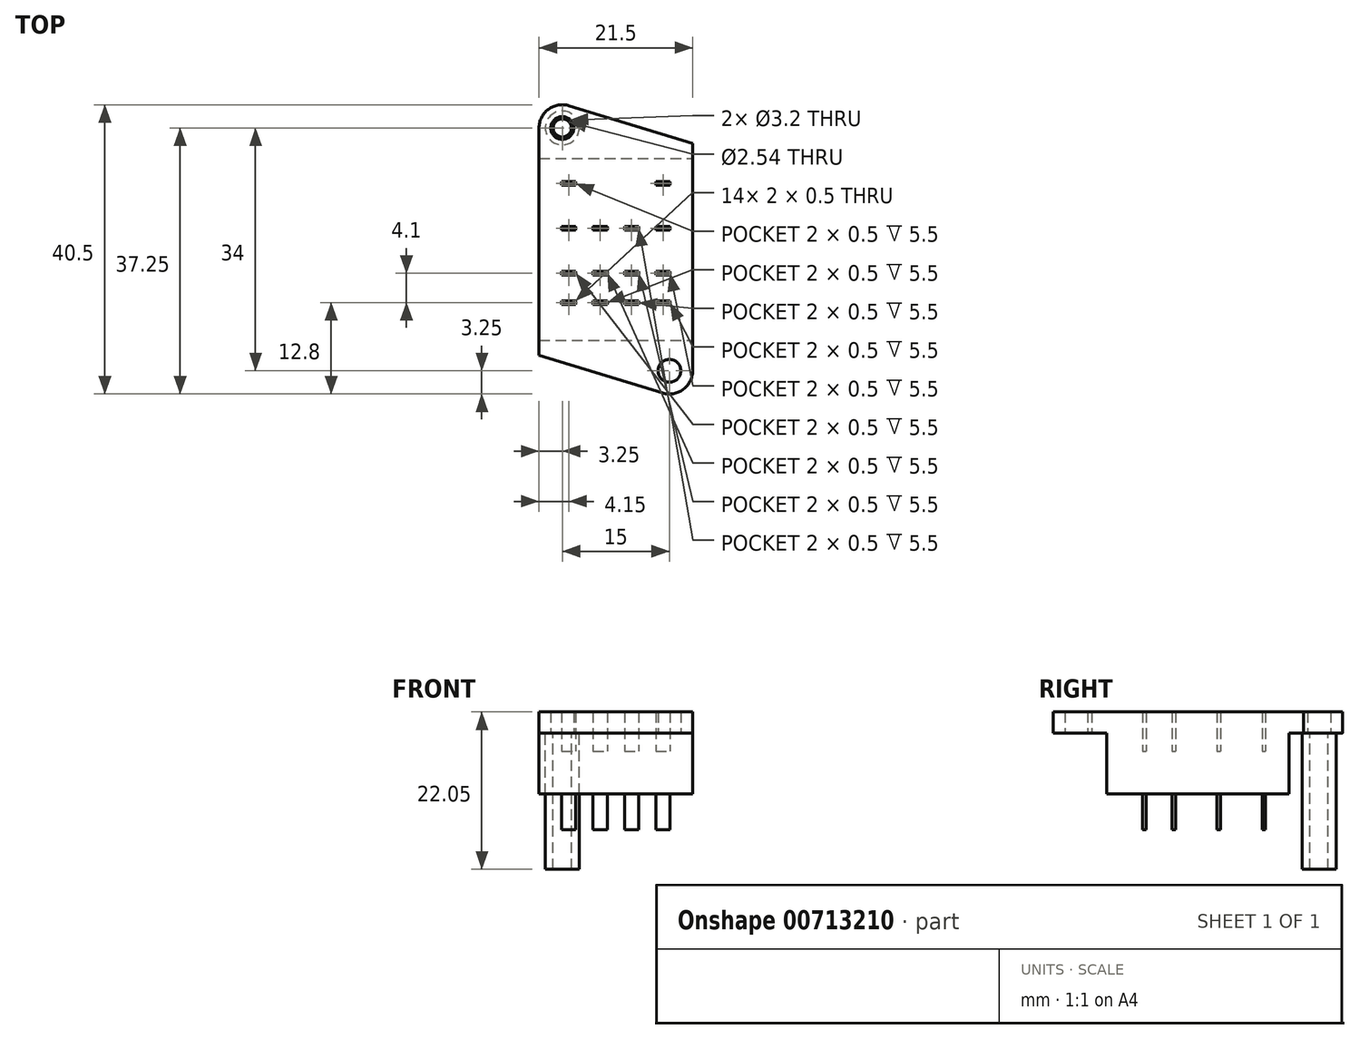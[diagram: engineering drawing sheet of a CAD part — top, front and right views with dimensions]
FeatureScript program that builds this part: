
annotation { "Feature Type Name" : "Feature", "Feature Type Description" : "" }
export const myFeature = defineFeature(function(context is Context, id is Id, definition is map)
    precondition{}
    {
        {
            var Q0;
            Q0=qCreatedBy(makeId("Top.planeOp"),FACE);
            var sketch = newSketch(context, id + "F0", { "sketchPlane" : qUnion([Q0])});
            skLineSegment(sketch, "E0", {"start": v(-10.75, 17) * mm, "end": v(-10.75, -14.82) * mm});
            skLineSegment(sketch, "E1", {"start": v(10.75, 14.82) * mm, "end": v(10.75, -17) * mm});
            skCircle(sketch, "E2", {"center": v(-7.5, 17) * mm, "radius": 1.6 * mm});
            skCircle(sketch, "E3", {"center": v(7.5, -17) * mm, "radius": 1.6 * mm});
            skArc(sketch, "E4", {"start": v(-10.75, 17) * mm, "mid": v(-9.43, 19.61) * mm, "end": v(-6.55, 20.1) * mm});
            skArc(sketch, "E5", {"start": v(10.75, -17) * mm, "mid": v(9.43, -19.61) * mm, "end": v(6.55, -20.1) * mm});
            skLineSegment(sketch, "E6", {"start": v(-10.75, -14.82) * mm, "end": v(6.55, -20.1) * mm});
            skLineSegment(sketch, "E7", {"start": v(-6.55, 20.1) * mm, "end": v(10.75, 14.82) * mm});
            skPoint(sketch, "E8.orphan", {"position": v(-10.75, -22.92) * mm});
            skPoint(sketch, "E9.orphan", {"position": v(15.75, -22.92) * mm});
            skSolve(sketch);
        }
        {
            var Q0;
            Q0 = qSketchRegion(id + "F0", true);
            extrude(context, id + "F1", {"entities" : qUnion([Q0]), "depth" : 3 * mm, "offsetDistance" : 25.4 * mm});
        }
        {
            var Q0;
            Q0=qCreatedBy(makeId("Top.planeOp"),FACE);
            var sketch = newSketch(context, id + "F2", { "sketchPlane" : qUnion([Q0])});
            skLineSegment(sketch, "E10.bottom", {"start": v(-10.75, 12.75) * mm, "end": v(10.75, 12.75) * mm});
            skLineSegment(sketch, "E10.top", {"start": v(-10.75, -12.75) * mm, "end": v(10.75, -12.75) * mm});
            skLineSegment(sketch, "E10.left", {"start": v(-10.75, 12.75) * mm, "end": v(-10.75, -12.75) * mm});
            skLineSegment(sketch, "E10.right", {"start": v(10.75, 12.75) * mm, "end": v(10.75, -12.75) * mm});
            skSolve(sketch);
        }
        {
            var Q0;
            Q0 = qSketchRegion(id + "F2", true);
            extrude(context, id + "F3", {"entities" : qUnion([Q0]), "operationType" : NewBodyOperationType.ADD, "oppositeDirection" : true, "depth" : 8.5 * mm, "offsetDistance" : 25.4 * mm});
        }
        {
            var Q0;
            Q0=makeQuery(id+"F3.opExtrude","CAP_FACE",FACE,{"disambiguationData":[OSD([sQuery(id+"F2.wireOp",EDGE,"E10.bottom"),sQuery(id+"F2.wireOp",EDGE,"E10.top"),sQuery(id+"F2.wireOp",EDGE,"E10.left"),sQuery(id+"F2.wireOp",EDGE,"E10.right")])],"isStart":false});
            var sketch = newSketch(context, id + "F4", { "sketchPlane" : qUnion([Q0])});
            skLineSegment(sketch, "E11.bottom", {"start": v(-7.6, 7.7) * mm, "end": v(-5.6, 7.7) * mm});
            skLineSegment(sketch, "E11.top", {"start": v(-7.6, 7.2) * mm, "end": v(-5.6, 7.2) * mm});
            skLineSegment(sketch, "E11.left", {"start": v(-7.6, 7.7) * mm, "end": v(-7.6, 7.2) * mm});
            skLineSegment(sketch, "E11.right", {"start": v(-5.6, 7.7) * mm, "end": v(-5.6, 7.2) * mm});
            skLineSegment(sketch, "E12", {"start": v(-7.6, 7.7) * mm, "end": v(-5.6, 7.2) * mm, "construction": true});
            skPoint(sketch, "E13", {"position": v(-6.6, 7.45) * mm});
            skLineSegment(sketch, "E14.1.0.0", {"start": v(-3.2, 7.7) * mm, "end": v(-3.2, 7.2) * mm});
            skLineSegment(sketch, "E14.1.0.1", {"start": v(-3.2, 7.7) * mm, "end": v(-1.2, 7.7) * mm});
            skLineSegment(sketch, "E14.1.0.2", {"start": v(-1.2, 7.7) * mm, "end": v(-1.2, 7.2) * mm});
            skLineSegment(sketch, "E14.1.0.3", {"start": v(-3.2, 7.2) * mm, "end": v(-1.2, 7.2) * mm});
            skLineSegment(sketch, "E14.2.0.0", {"start": v(1.2, 7.7) * mm, "end": v(1.2, 7.2) * mm});
            skLineSegment(sketch, "E14.2.0.1", {"start": v(1.2, 7.7) * mm, "end": v(3.2, 7.7) * mm});
            skLineSegment(sketch, "E14.2.0.2", {"start": v(3.2, 7.7) * mm, "end": v(3.2, 7.2) * mm});
            skLineSegment(sketch, "E14.2.0.3", {"start": v(1.2, 7.2) * mm, "end": v(3.2, 7.2) * mm});
            skLineSegment(sketch, "E14.3.0.0", {"start": v(5.6, 7.7) * mm, "end": v(5.6, 7.2) * mm});
            skLineSegment(sketch, "E14.3.0.1", {"start": v(5.6, 7.7) * mm, "end": v(7.6, 7.7) * mm});
            skLineSegment(sketch, "E14.3.0.2", {"start": v(7.6, 7.7) * mm, "end": v(7.6, 7.2) * mm});
            skLineSegment(sketch, "E14.3.0.3", {"start": v(5.6, 7.2) * mm, "end": v(7.6, 7.2) * mm});
            skLineSegment(sketch, "E14.direction1", {"start": v(-7.6, 7.2) * mm, "end": v(-3.2, 7.2) * mm, "construction": true});
            skLineSegment(sketch, "E15.1.0.0", {"start": v(5.6, 3.6) * mm, "end": v(7.6, 3.6) * mm});
            skLineSegment(sketch, "E15.1.0.1", {"start": v(5.6, 3.1) * mm, "end": v(7.6, 3.1) * mm});
            skLineSegment(sketch, "E15.1.0.2", {"start": v(-7.6, 3.6) * mm, "end": v(-5.6, 3.6) * mm});
            skLineSegment(sketch, "E15.1.0.3", {"start": v(-3.2, 3.6) * mm, "end": v(-1.2, 3.6) * mm});
            skLineSegment(sketch, "E15.1.0.4", {"start": v(-3.2, 3.1) * mm, "end": v(-1.2, 3.1) * mm});
            skLineSegment(sketch, "E15.1.0.5", {"start": v(1.2, 3.6) * mm, "end": v(3.2, 3.6) * mm});
            skLineSegment(sketch, "E15.1.0.6", {"start": v(1.2, 3.1) * mm, "end": v(3.2, 3.1) * mm});
            skLineSegment(sketch, "E15.1.0.7", {"start": v(-7.6, 3.1) * mm, "end": v(-3.2, 3.1) * mm, "construction": true});
            skLineSegment(sketch, "E15.1.0.8", {"start": v(-7.6, 3.1) * mm, "end": v(-5.6, 3.1) * mm});
            skLineSegment(sketch, "E15.1.0.9", {"start": v(7.6, 3.6) * mm, "end": v(7.6, 3.1) * mm});
            skLineSegment(sketch, "E15.1.0.10", {"start": v(5.6, 3.6) * mm, "end": v(5.6, 3.1) * mm});
            skLineSegment(sketch, "E15.1.0.11", {"start": v(-5.6, 3.6) * mm, "end": v(-5.6, 3.1) * mm});
            skLineSegment(sketch, "E15.1.0.12", {"start": v(-3.2, 3.6) * mm, "end": v(-3.2, 3.1) * mm});
            skLineSegment(sketch, "E15.1.0.13", {"start": v(-1.2, 3.6) * mm, "end": v(-1.2, 3.1) * mm});
            skLineSegment(sketch, "E15.1.0.14", {"start": v(1.2, 3.6) * mm, "end": v(1.2, 3.1) * mm});
            skLineSegment(sketch, "E15.1.0.15", {"start": v(3.2, 3.6) * mm, "end": v(3.2, 3.1) * mm});
            skLineSegment(sketch, "E15.1.0.16", {"start": v(-7.6, 3.6) * mm, "end": v(-7.6, 3.1) * mm});
            skLineSegment(sketch, "E15.direction1", {"start": v(-7.6, 7.2) * mm, "end": v(-7.6, 3.1) * mm, "construction": true});
            skLineSegment(sketch, "E16.1.0.0", {"start": v(1.2, -3.2) * mm, "end": v(3.2, -3.2) * mm});
            skLineSegment(sketch, "E16.1.0.1", {"start": v(-3.2, -2.7) * mm, "end": v(-1.2, -2.7) * mm});
            skLineSegment(sketch, "E16.1.0.2", {"start": v(-3.2, -3.2) * mm, "end": v(-1.2, -3.2) * mm});
            skLineSegment(sketch, "E16.1.0.3", {"start": v(-7.6, -3.2) * mm, "end": v(-3.2, -3.2) * mm, "construction": true});
            skLineSegment(sketch, "E16.1.0.4", {"start": v(5.6, -2.7) * mm, "end": v(7.6, -2.7) * mm});
            skLineSegment(sketch, "E16.1.0.5", {"start": v(1.2, -2.7) * mm, "end": v(3.2, -2.7) * mm});
            skLineSegment(sketch, "E16.1.0.6", {"start": v(-7.6, -2.7) * mm, "end": v(-5.6, -2.7) * mm});
            skLineSegment(sketch, "E16.1.0.7", {"start": v(5.6, -3.2) * mm, "end": v(7.6, -3.2) * mm});
            skLineSegment(sketch, "E16.1.0.8", {"start": v(-7.6, 0.9) * mm, "end": v(-7.6, -3.2) * mm, "construction": true});
            skLineSegment(sketch, "E16.1.0.9", {"start": v(-7.6, -3.2) * mm, "end": v(-5.6, -3.2) * mm});
            skLineSegment(sketch, "E16.1.0.10", {"start": v(5.6, -2.7) * mm, "end": v(5.6, -3.2) * mm});
            skLineSegment(sketch, "E16.1.0.11", {"start": v(-3.2, -2.7) * mm, "end": v(-3.2, -3.2) * mm});
            skLineSegment(sketch, "E16.1.0.12", {"start": v(3.2, -2.7) * mm, "end": v(3.2, -3.2) * mm});
            skLineSegment(sketch, "E16.1.0.13", {"start": v(-1.2, -2.7) * mm, "end": v(-1.2, -3.2) * mm});
            skLineSegment(sketch, "E16.1.0.14", {"start": v(-7.6, -2.7) * mm, "end": v(-7.6, -3.2) * mm});
            skLineSegment(sketch, "E16.1.0.15", {"start": v(-5.6, -2.7) * mm, "end": v(-5.6, -3.2) * mm});
            skLineSegment(sketch, "E16.1.0.16", {"start": v(7.6, -2.7) * mm, "end": v(7.6, -3.2) * mm});
            skLineSegment(sketch, "E16.1.0.17", {"start": v(1.2, -2.7) * mm, "end": v(1.2, -3.2) * mm});
            skLineSegment(sketch, "E16.2.0.4", {"start": v(5.6, -9) * mm, "end": v(7.6, -9) * mm});
            skLineSegment(sketch, "E16.2.0.6", {"start": v(-7.6, -9) * mm, "end": v(-5.6, -9) * mm});
            skLineSegment(sketch, "E16.2.0.7", {"start": v(5.6, -9.5) * mm, "end": v(7.6, -9.5) * mm});
            skLineSegment(sketch, "E16.2.0.8", {"start": v(-7.6, -5.4) * mm, "end": v(-7.6, -9.5) * mm, "construction": true});
            skLineSegment(sketch, "E16.2.0.9", {"start": v(-7.6, -9.5) * mm, "end": v(-5.6, -9.5) * mm});
            skLineSegment(sketch, "E16.2.0.10", {"start": v(5.6, -9) * mm, "end": v(5.6, -9.5) * mm});
            skLineSegment(sketch, "E16.2.0.14", {"start": v(-7.6, -9) * mm, "end": v(-7.6, -9.5) * mm});
            skLineSegment(sketch, "E16.2.0.15", {"start": v(-5.6, -9) * mm, "end": v(-5.6, -9.5) * mm});
            skLineSegment(sketch, "E16.2.0.16", {"start": v(7.6, -9) * mm, "end": v(7.6, -9.5) * mm});
            skLineSegment(sketch, "E16.direction1", {"start": v(-7.6, 3.1) * mm, "end": v(-7.6, -3.2) * mm, "construction": true});
            skSolve(sketch);
        }
        {
            var Q0;
            Q0 = qSketchRegion(id + "F4", true);
            extrude(context, id + "F5", {"entities" : qUnion([Q0]), "operationType" : NewBodyOperationType.ADD, "depth" : 5 * mm, "offsetDistance" : 25.4 * mm});
        }
        {
            var Q0;
            Q0 = qSketchRegion(id + "F4", true);
            var Q1;
            Q1=makeQuery(id+"F1.opExtrude","CAP_FACE",FACE,{"disambiguationData":[OSD([sQuery(id+"F0.wireOp",EDGE,"E0"),sQuery(id+"F0.wireOp",EDGE,"E1"),sQuery(id+"F0.wireOp",EDGE,"E2"),sQuery(id+"F0.wireOp",EDGE,"E3"),sQuery(id+"F0.wireOp",EDGE,"E4"),sQuery(id+"F0.wireOp",EDGE,"E5"),sQuery(id+"F0.wireOp",EDGE,"E6"),sQuery(id+"F0.wireOp",EDGE,"E7")])],"isStart":false});
            extrude(context, id + "F6", {"entities" : qUnion([Q0]), "operationType" : NewBodyOperationType.REMOVE, "endBound" : BoundingType.UP_TO_SURFACE, "oppositeDirection" : true, "depth" : 25.4 * mm, "endBoundEntityFace" : qUnion([Q1]), "offsetDistance" : 25.4 * mm, "hasSecondDirection" : true, "secondDirectionOppositeDirection" : true, "secondDirectionDepth" : 6 * mm});
        }
        {
            var Q0;
            Q0=qCreatedBy(makeId("Top.planeOp"),FACE);
            var sketch = newSketch(context, id + "F7", { "sketchPlane" : qUnion([Q0])});
            skCircle(sketch, "E17", {"center": v(-7.5, 17) * mm, "radius": 2.37 * mm});
            skCircle(sketch, "E18", {"center": v(-7.5, 17) * mm, "radius": 1.27 * mm});
            skSolve(sketch);
        }
        {
            var Q0;
            Q0 = qSketchRegion(id + "F7", true);
            extrude(context, id + "F8", {"entities" : qUnion([Q0]), "oppositeDirection" : true, "depth" : 19.05 * mm, "offsetDistance" : 25.4 * mm});
        }
    });
